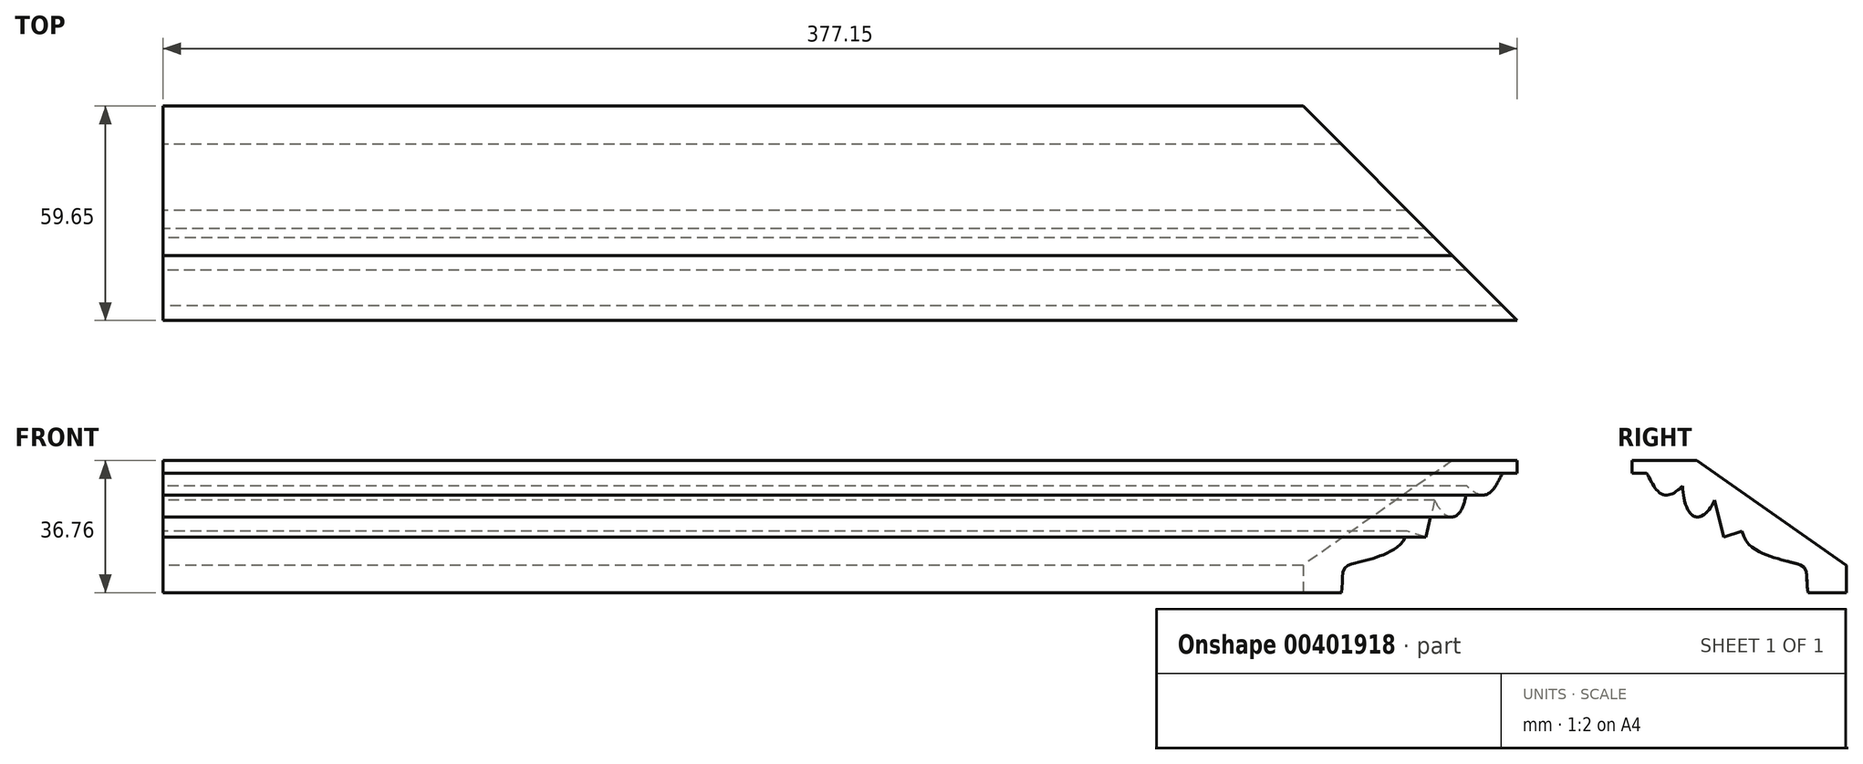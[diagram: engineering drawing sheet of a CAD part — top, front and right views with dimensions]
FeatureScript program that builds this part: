
annotation { "Feature Type Name" : "Feature", "Feature Type Description" : "" }
export const myFeature = defineFeature(function(context is Context, id is Id, definition is map)
    precondition{}
    {
        {
            var Q0;
            Q0=qCreatedBy(makeId("Right.planeOp"),FACE);
            var sketch = newSketch(context, id + "F0", { "sketchPlane" : qUnion([Q0])});
            skLineSegment(sketch, "E0", {"start": v(0, 7.62) * mm, "end": v(-41.61, 36.76) * mm});
            skLineSegment(sketch, "E1", {"start": v(-41.61, 36.76) * mm, "end": v(-59.65, 36.76) * mm});
            skLineSegment(sketch, "E2", {"start": v(-59.65, 36.76) * mm, "end": v(-59.65, 33.27) * mm});
            skLineSegment(sketch, "E3", {"start": v(-59.65, 33.27) * mm, "end": v(-55.58, 33.27) * mm});
            skLineSegment(sketch, "E4", {"start": v(0, 7.62) * mm, "end": v(0, 0) * mm});
            skLineSegment(sketch, "E5", {"start": v(0, 0) * mm, "end": v(-10.67, 0) * mm});
            skFitSpline(sketch, "E6", {"points": [v(-10.67, 0) * mm, v(-11.13, 5.86) * mm, v(-13.39, 7.89) * mm, v(-29.01, 17.09) * mm], "startDerivative": vector(-5.08, 29.03) * mm, "endDerivative": vector(-6.54, 39.72) * mm});
            skLineSegment(sketch, "E7", {"start": v(-29.01, 17.09) * mm, "end": v(-34.16, 15.48) * mm});
            skLineSegment(sketch, "E8", {"start": v(-34.16, 15.48) * mm, "end": v(-36.66, 25.7) * mm});
            skFitSpline(sketch, "E9", {"points": [v(-45.63, 29.67) * mm, v(-52.53, 28.3) * mm, v(-55.58, 33.27) * mm], "startDerivative": vector(-24.15, -24.15) * mm, "endDerivative": vector(-16.65, 31.11) * mm});
            skFitSpline(sketch, "E10", {"points": [v(-45.63, 29.67) * mm, v(-36.66, 25.7) * mm], "startDerivative": vector(2.07, -32.09) * mm, "endDerivative": vector(9.32, 20.18) * mm});
            skSolve(sketch);
        }
        {
            var Q0;
            Q0=qSketchRegion(id+"F0",true);
            var Q1;
            Q1=qSketchRegion(id+"F2",true);
            extrude(context, id + "F1", {"entities" : qUnion([Q0, Q1]), "depth" : 177.8 * mm, "hasSecondDirection" : true, "secondDirectionOppositeDirection" : true, "secondDirectionDepth" : 228.6 * mm});
        }
        {
            var Q0;
            Q0=qCreatedBy(makeId("Top.planeOp"),FACE);
            var sketch = newSketch(context, id + "F2", { "sketchPlane" : qUnion([Q0])});
            skLineSegment(sketch, "E11", {"start": v(-88.9, 0) * mm, "end": v(88.9, 0) * mm, "construction": true});
            skLineSegment(sketch, "E12", {"start": v(88.9, 0) * mm, "end": v(184.11, 0) * mm});
            skLineSegment(sketch, "E13", {"start": v(184.11, 0) * mm, "end": v(184.11, -95.21) * mm});
            skLineSegment(sketch, "E14", {"start": v(184.11, -95.21) * mm, "end": v(88.9, 0) * mm});
            skLineSegment(sketch, "E15", {"start": v(0, 0) * mm, "end": v(0, -141.75) * mm, "construction": true});
            skSolve(sketch);
        }
        {
            var Q0;
            Q0=qSketchRegion(id+"F2",true);
            extrude(context, id + "F3", {"entities" : qUnion([Q0]), "operationType" : NewBodyOperationType.REMOVE, "endBound" : BoundingType.THROUGH_ALL, "depth" : 25.4 * mm});
        }
    });
